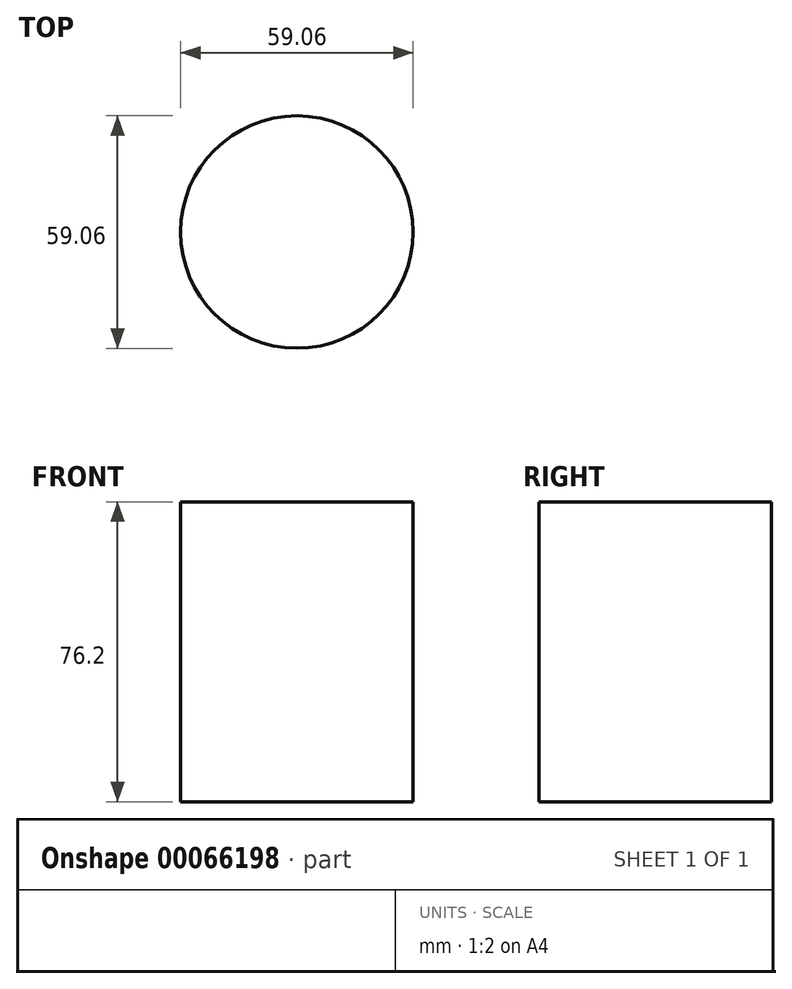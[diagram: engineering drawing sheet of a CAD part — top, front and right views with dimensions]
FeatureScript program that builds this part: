
annotation { "Feature Type Name" : "Feature", "Feature Type Description" : "" }
export const myFeature = defineFeature(function(context is Context, id is Id, definition is map)
    precondition{}
    {
        {
            var Q0;
            Q0=qCreatedBy(makeId("Top.planeOp"),FACE);
            var sketch = newSketch(context, id + "F0", { "sketchPlane" : qUnion([Q0])});
            skCircle(sketch, "E0", {"center": v(0, 0) * mm, "radius": 29.61 * mm});
            skCircle(sketch, "E1", {"center": v(0, 0) * mm, "radius": 29.53 * mm});
            skSolve(sketch);
        }
        {
            var Q0;
            Q0=makeQuery(id+"F0.imprint","IMPRINT",FACE,{"disambiguationData":[TD([[makeQuery(id+"F0.imprint","IMPRINT",EDGE,{"derivedFrom":sQuery(id+"F0.wireOp",EDGE,"E1")}),1.0]])]});
            extrude(context, id + "F1", {"entities" : qUnion([Q0]), "depth" : 76.2 * mm});
        }
    });
